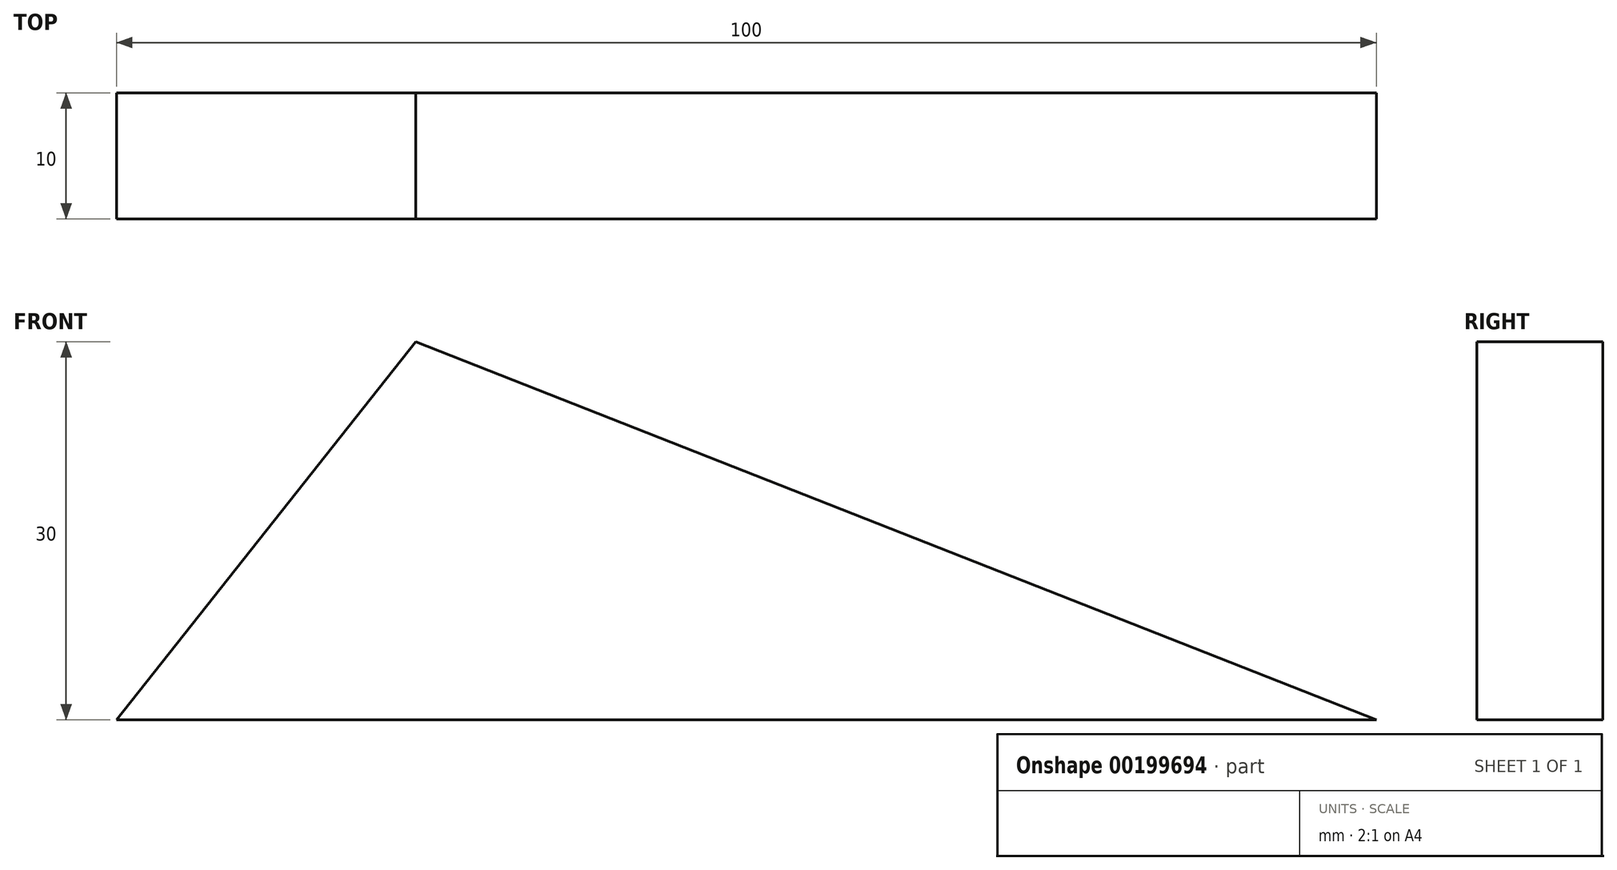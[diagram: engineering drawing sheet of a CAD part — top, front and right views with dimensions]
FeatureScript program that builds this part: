
annotation { "Feature Type Name" : "Feature", "Feature Type Description" : "" }
export const myFeature = defineFeature(function(context is Context, id is Id, definition is map)
    precondition{}
    {
        {
            var Q0;
            Q0=qCreatedBy(makeId("Front.planeOp"),FACE);
            var sketch = newSketch(context, id + "F0", { "sketchPlane" : qUnion([Q0])});
            skLineSegment(sketch, "E0", {"start": v(-50, 0) * mm, "end": v(50, 0) * mm});
            skLineSegment(sketch, "E1", {"start": v(-50, 0) * mm, "end": v(-26.25, 30) * mm});
            skLineSegment(sketch, "E2", {"start": v(-26.25, 30) * mm, "end": v(50, 0) * mm});
            skLineSegment(sketch, "E3", {"start": v(-50, 30) * mm, "end": v(50, 30) * mm, "construction": true});
            skLineSegment(sketch, "E4", {"start": v(-50, 0) * mm, "end": v(-50, 30) * mm, "construction": true});
            skLineSegment(sketch, "E5", {"start": v(50, 0) * mm, "end": v(50, 30) * mm, "construction": true});
            skPoint(sketch, "E6", {"position": v(0, 30) * mm});
            skSolve(sketch);
        }
        {
            var Q0;
            Q0 = qSketchRegion(id + "F0", true);
            extrude(context, id + "F1", {"entities" : qUnion([Q0]), "oppositeDirection" : true, "depth" : 10 * mm, "offsetDistance" : 25 * mm});
        }
    });
